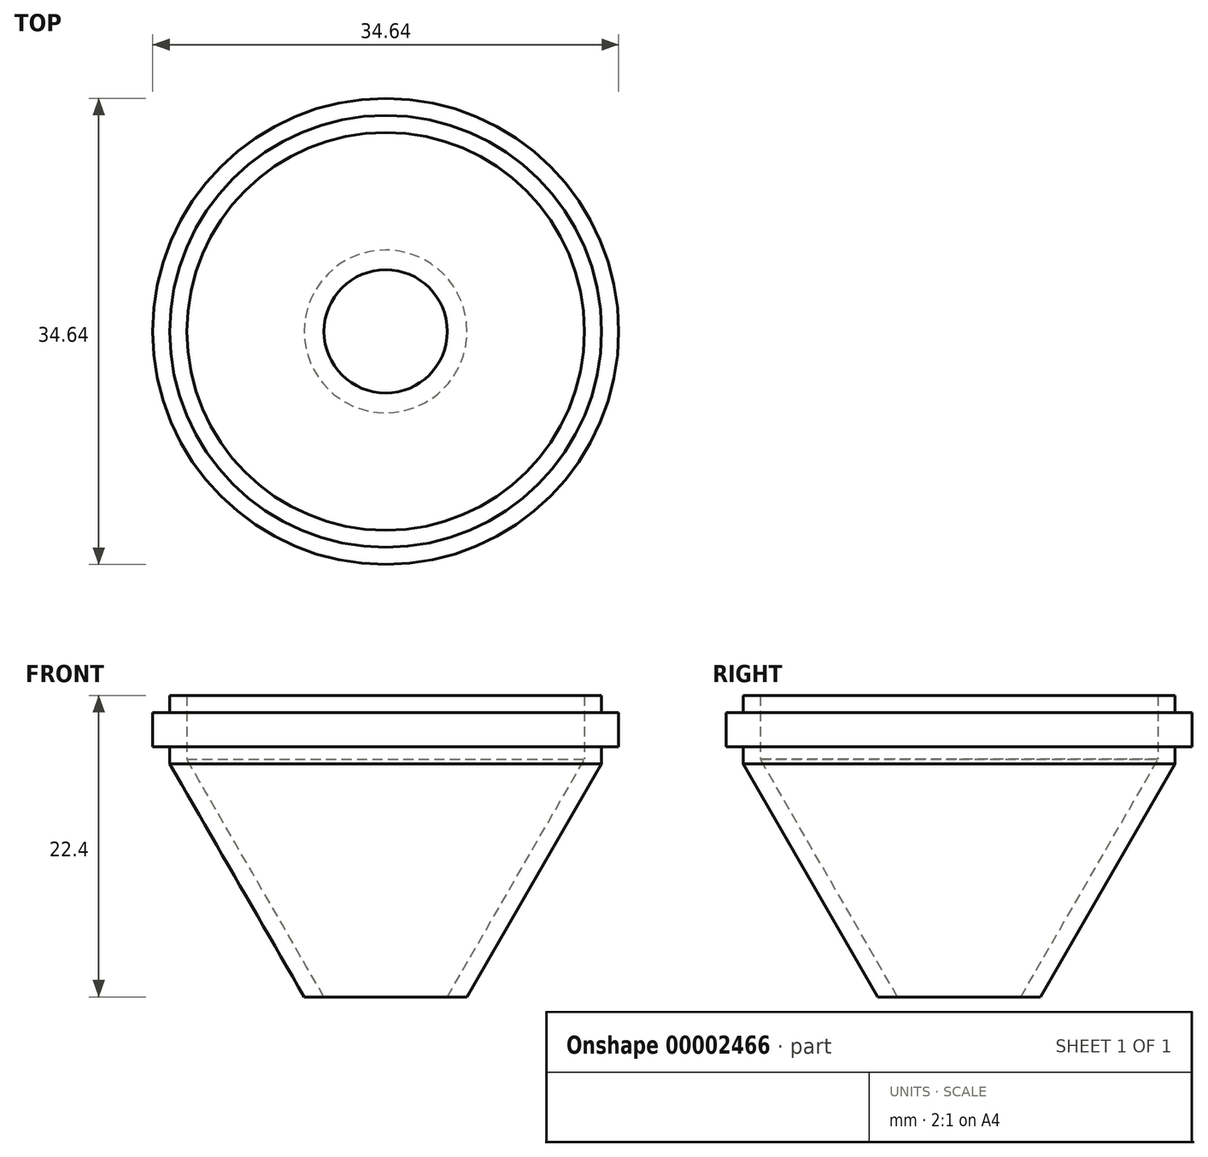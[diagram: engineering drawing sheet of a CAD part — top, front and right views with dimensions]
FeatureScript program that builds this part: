
annotation { "Feature Type Name" : "Feature", "Feature Type Description" : "" }
export const myFeature = defineFeature(function(context is Context, id is Id, definition is map)
    precondition{}
    {
        {
            var Q0;
            Q0=qCreatedBy(makeId("Front.planeOp"),FACE);
            var sketch = newSketch(context, id + "F0", { "sketchPlane" : qUnion([Q0])});
            skLineSegment(sketch, "E0", {"start": v(16.05, 0) * mm, "end": v(16.05, -1.27) * mm});
            skLineSegment(sketch, "E1", {"start": v(16.05, -5.08) * mm, "end": v(6.05, -22.4) * mm});
            skLineSegment(sketch, "E2", {"start": v(4.58, -22.4) * mm, "end": v(14.78, -4.74) * mm});
            skLineSegment(sketch, "E3", {"start": v(14.78, -4.74) * mm, "end": v(14.78, 0) * mm});
            skLineSegment(sketch, "E4", {"start": v(14.78, 0) * mm, "end": v(16.05, 0) * mm});
            skLineSegment(sketch, "E5", {"start": v(17.32, -3.81) * mm, "end": v(16.05, -3.81) * mm});
            skLineSegment(sketch, "E6", {"start": v(16.05, -1.27) * mm, "end": v(17.32, -1.27) * mm});
            skLineSegment(sketch, "E7", {"start": v(17.32, -1.27) * mm, "end": v(17.32, -3.81) * mm});
            skLineSegment(sketch, "E8.trimOffspring", {"start": v(16.05, -3.81) * mm, "end": v(16.05, -5.08) * mm});
            skLineSegment(sketch, "E9", {"start": v(4.58, -22.4) * mm, "end": v(6.05, -22.4) * mm});
            skSolve(sketch);
        }
        {
            var Q0;
            Q0=qCreatedBy(makeId("Front.planeOp"),FACE);
            var sketch = newSketch(context, id + "F1", { "sketchPlane" : qUnion([Q0])});
            skLineSegment(sketch, "E10", {"start": v(0, -29.45) * mm, "end": v(0, 0) * mm});
            skSolve(sketch);
        }
        {
            var Q0;
            Q0=makeQuery(id+"F0.imprint","IMPRINT",FACE,{"disambiguationData":[TD([[makeQuery(id+"F0.imprint","IMPRINT",EDGE,{"derivedFrom":sQuery(id+"F0.wireOp",EDGE,"E0")}),-1.0]])]});
            var Q1;
            Q1=makeQuery(id+"F0.imprint","IMPRINT",FACE,{"disambiguationData":[TD([[makeQuery(id+"F0.imprint","IMPRINT",EDGE,{"derivedFrom":sQuery(id+"F0.wireOp",EDGE,"913fc122-1195-4bdb-b6a9-ddf004c25220")}),1.0]])]});
            var Q2;
            Q2=sQuery(id+"F1.wireOp",EDGE,"E10");
            revolve(context, id + "F2", {"entities" : qUnion([Q0, Q1]), "axis" : qUnion([Q2]), "revolveType" : RevolveType.FULL});
        }
    });
